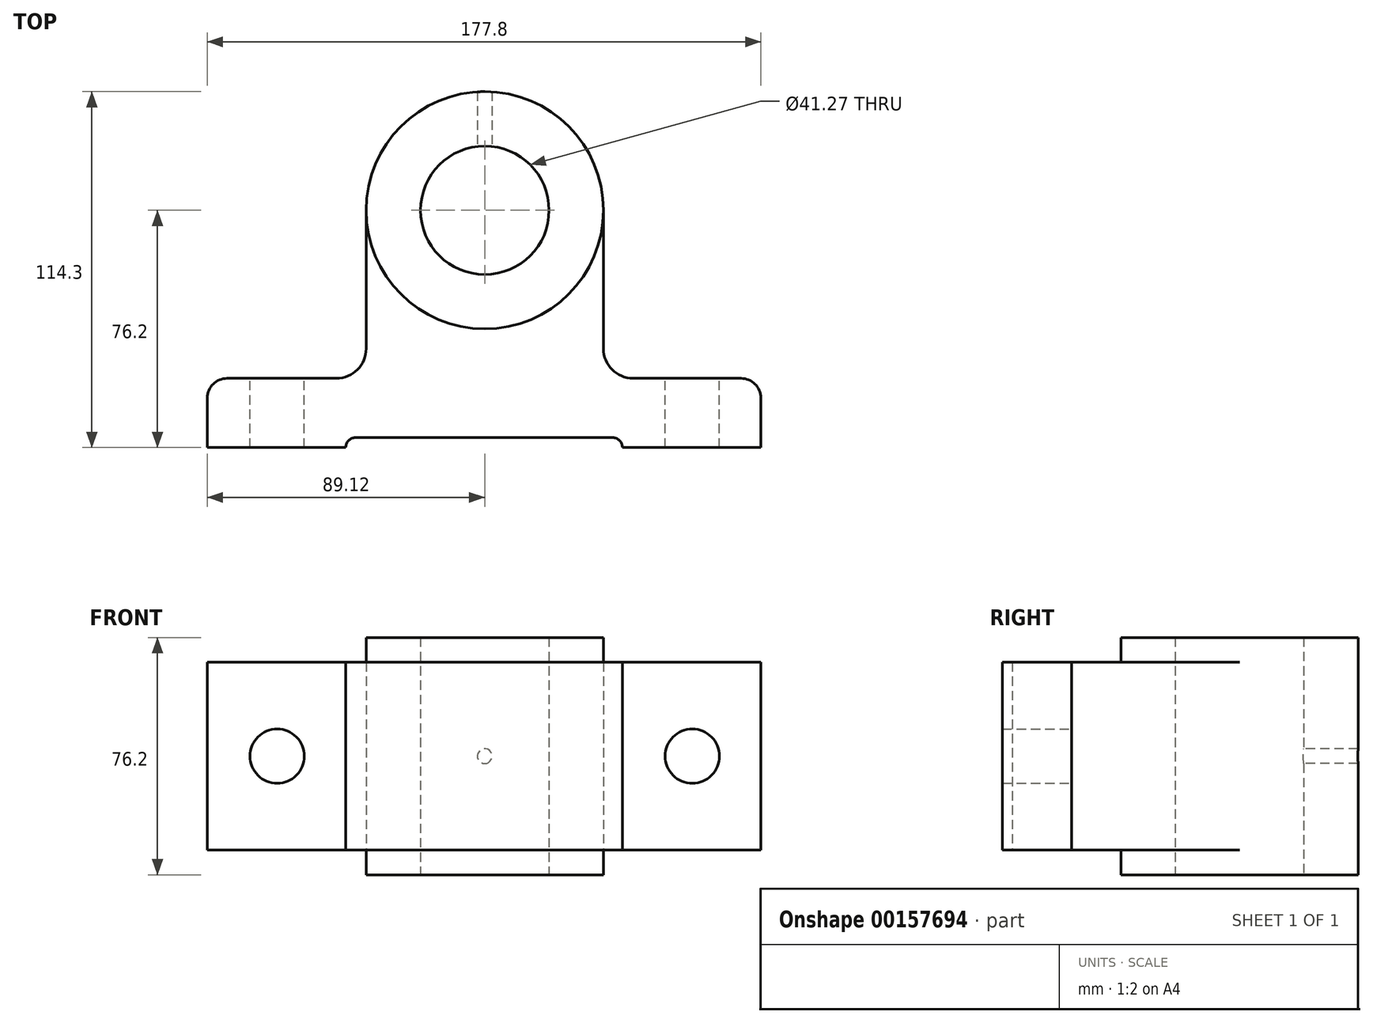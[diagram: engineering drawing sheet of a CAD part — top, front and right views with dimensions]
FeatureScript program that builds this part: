
annotation { "Feature Type Name" : "Feature", "Feature Type Description" : "" }
export const myFeature = defineFeature(function(context is Context, id is Id, definition is map)
    precondition{}
    {
        {
            var Q0;
            Q0=qCreatedBy(makeId("Top.planeOp"),FACE);
            var sketch = newSketch(context, id + "F0", { "sketchPlane" : qUnion([Q0])});
            skLineSegment(sketch, "E0", {"start": v(0, 92.13) * mm, "end": v(0, -91.9) * mm});
            skLineSegment(sketch, "E1.0", {"start": v(-89.12, -76.2) * mm, "end": v(-44.67, -76.2) * mm});
            skLineSegment(sketch, "E2", {"start": v(88.68, -76.2) * mm, "end": v(44.23, -76.2) * mm});
            skLineSegment(sketch, "E3.0", {"start": v(-41.5, -73.02) * mm, "end": v(41.05, -73.02) * mm});
            skLineSegment(sketch, "E4", {"start": v(-44.67, -76.2) * mm, "end": v(-44.67, -76.2) * mm});
            skLineSegment(sketch, "E5", {"start": v(44.23, -76.2) * mm, "end": v(44.23, -76.2) * mm});
            skLineSegment(sketch, "E6.trimOffspring", {"start": v(44.23, -76.2) * mm, "end": v(88.68, -76.2) * mm});
            skPoint(sketch, "E7.visualSharp", {"position": v(44.23, -73.02) * mm});
            skArc(sketch, "E7.filletArc", {"start": v(44.23, -76.2) * mm, "mid": v(43.3, -73.95) * mm, "end": v(41.05, -73.02) * mm});
            skPoint(sketch, "E8.visualSharp", {"position": v(-44.67, -73.02) * mm});
            skArc(sketch, "E8.filletArc", {"start": v(-41.5, -73.02) * mm, "mid": v(-43.74, -73.95) * mm, "end": v(-44.67, -76.2) * mm});
            skLineSegment(sketch, "E9.0", {"start": v(47.63, -53.97) * mm, "end": v(82.33, -53.97) * mm});
            skLineSegment(sketch, "E10.0", {"start": v(-82.77, -53.97) * mm, "end": v(-47.62, -53.97) * mm});
            skLineSegment(sketch, "E11", {"start": v(-89.12, -60.32) * mm, "end": v(-89.12, -76.2) * mm});
            skLineSegment(sketch, "E12", {"start": v(88.68, -60.32) * mm, "end": v(88.68, -76.2) * mm});
            skPoint(sketch, "E13.visualSharp", {"position": v(88.68, -53.97) * mm});
            skArc(sketch, "E13.filletArc", {"start": v(88.68, -60.32) * mm, "mid": v(86.82, -55.83) * mm, "end": v(82.33, -53.97) * mm});
            skPoint(sketch, "E14.visualSharp", {"position": v(-89.12, -53.97) * mm});
            skArc(sketch, "E14.filletArc", {"start": v(-82.77, -53.97) * mm, "mid": v(-87.26, -55.83) * mm, "end": v(-89.12, -60.32) * mm});
            skLineSegment(sketch, "E15", {"start": v(-38.1, -44.45) * mm, "end": v(-38.1, 0) * mm});
            skLineSegment(sketch, "E16", {"start": v(38.1, -44.45) * mm, "end": v(38.1, 0) * mm});
            skPoint(sketch, "E17.visualSharp", {"position": v(38.1, -53.97) * mm});
            skArc(sketch, "E17.filletArc", {"start": v(38.1, -44.45) * mm, "mid": v(40.89, -51.19) * mm, "end": v(47.63, -53.97) * mm});
            skPoint(sketch, "E18.visualSharp", {"position": v(-38.1, -53.97) * mm});
            skArc(sketch, "E18.filletArc", {"start": v(-47.62, -53.97) * mm, "mid": v(-40.89, -51.19) * mm, "end": v(-38.1, -44.45) * mm});
            skArc(sketch, "E19", {"start": v(-38.1, 0) * mm, "mid": v(0, -38.1) * mm, "end": v(38.1, 0) * mm});
            skSolve(sketch);
        }
        {
            var Q0;
            Q0=qCreatedBy(makeId("Top.planeOp"),FACE);
            var sketch = newSketch(context, id + "F1", { "sketchPlane" : qUnion([Q0])});
            skCircle(sketch, "E20", {"center": v(0, 0) * mm, "radius": 38.1 * mm});
            skCircle(sketch, "E21", {"center": v(0, 0) * mm, "radius": 26.99 * mm});
            skCircle(sketch, "E22", {"center": v(0, 0) * mm, "radius": 20.64 * mm});
            skSolve(sketch);
        }
        {
            var Q0;
            Q0=makeQuery(id+"F1.imprint","IMPRINT",FACE,{"disambiguationData":[TD([[makeQuery(id+"F1.imprint","IMPRINT",EDGE,{"derivedFrom":sQuery(id+"F1.wireOp",EDGE,"E20")}),1.0]])]});
            var Q1;
            Q1=makeQuery(id+"F1.imprint","IMPRINT",FACE,{"disambiguationData":[TD([[makeQuery(id+"F1.imprint","IMPRINT",EDGE,{"derivedFrom":sQuery(id+"F1.wireOp",EDGE,"E21")}),1.0]])]});
            extrude(context, id + "F2", {"entities" : qUnion([Q0, Q1]), "endBound" : BoundingType.SYMMETRIC, "depth" : 76.2 * mm});
        }
        {
            var Q0;
            Q0 = qSketchRegion(id + "F0", true);
            extrude(context, id + "F3", {"entities" : qUnion([Q0]), "operationType" : NewBodyOperationType.ADD, "endBound" : BoundingType.SYMMETRIC, "depth" : 60.32 * mm});
        }
        {
            var Q0;
            Q0=qCreatedBy(makeId("Front.planeOp"),FACE);
            var sketch = newSketch(context, id + "F4", { "sketchPlane" : qUnion([Q0])});
            skCircle(sketch, "E23", {"center": v(-66.68, 0) * mm, "radius": 8.72 * mm});
            skCircle(sketch, "E24", {"center": v(66.68, 0) * mm, "radius": 8.72 * mm});
            skSolve(sketch);
        }
        {
            var Q0;
            Q0 = qSketchRegion(id + "F4", true);
            extrude(context, id + "F5", {"entities" : qUnion([Q0]), "operationType" : NewBodyOperationType.REMOVE, "depth" : 254 * mm});
        }
        {
            var Q0;
            Q0=qCreatedBy(makeId("Front.planeOp"),FACE);
            var sketch = newSketch(context, id + "F6", { "sketchPlane" : qUnion([Q0])});
            skCircle(sketch, "E25", {"center": v(0, 0) * mm, "radius": 2.37 * mm});
            skSolve(sketch);
        }
        {
            var Q0;
            Q0 = qSketchRegion(id + "F6", true);
            extrude(context, id + "F7", {"entities" : qUnion([Q0]), "operationType" : NewBodyOperationType.REMOVE, "oppositeDirection" : true, "depth" : 50.8 * mm});
        }
    });
